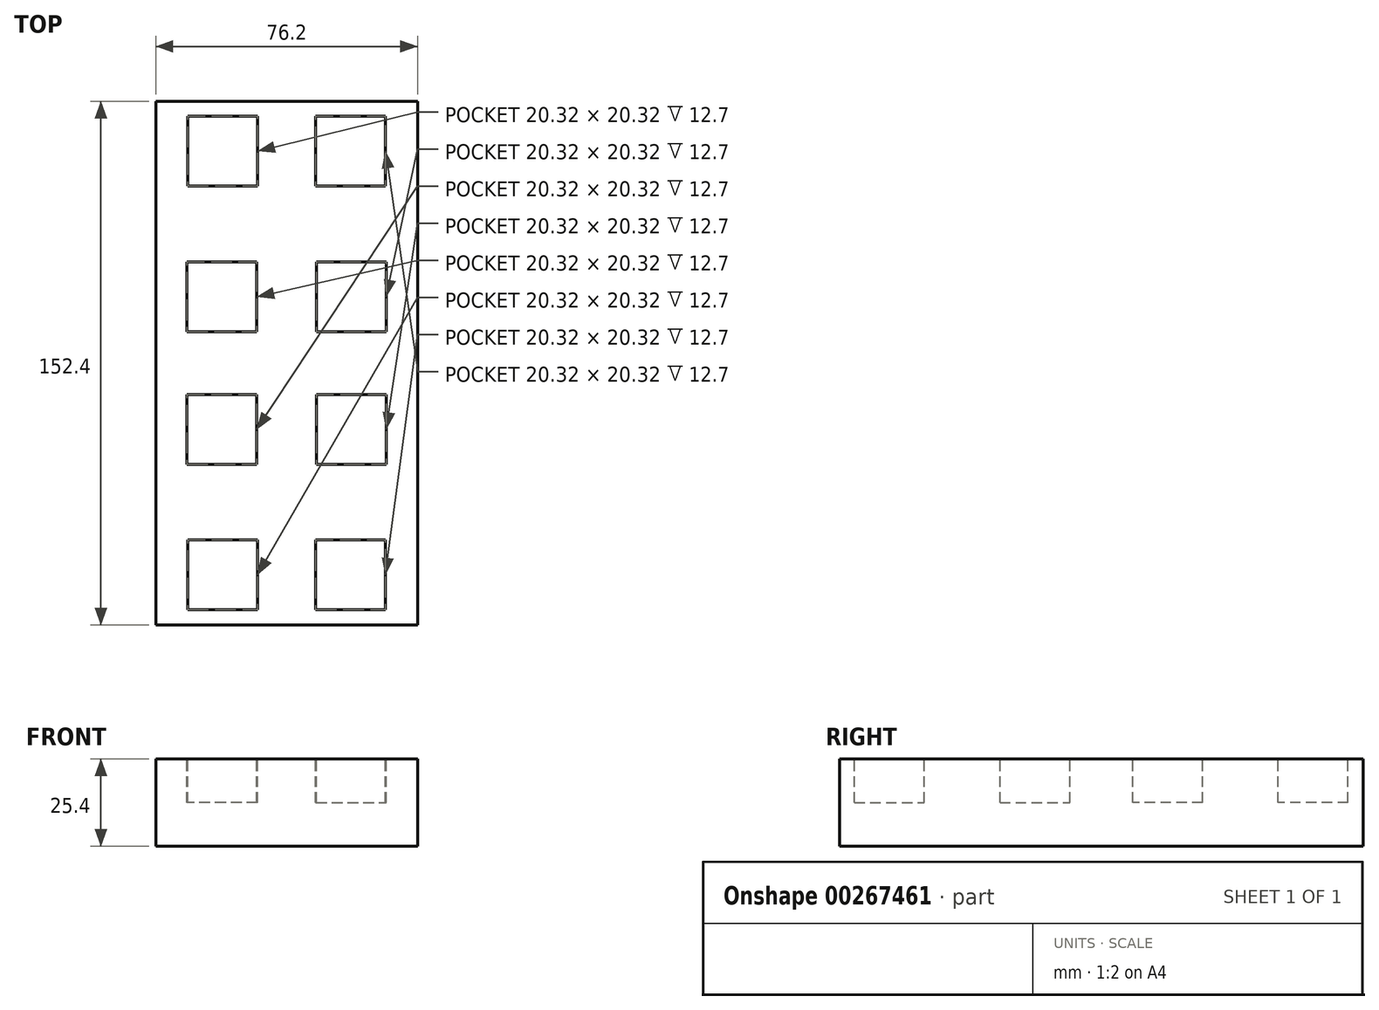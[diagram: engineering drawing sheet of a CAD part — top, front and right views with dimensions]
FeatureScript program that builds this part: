
annotation { "Feature Type Name" : "Feature", "Feature Type Description" : "" }
export const myFeature = defineFeature(function(context is Context, id is Id, definition is map)
    precondition{}
    {
        {
            var Q0;
            Q0=qCreatedBy(makeId("Top.planeOp"),FACE);
            var sketch = newSketch(context, id + "F0", { "sketchPlane" : qUnion([Q0])});
            skLineSegment(sketch, "E0.bottom", {"start": v(38.1, 76.2) * mm, "end": v(-38.1, 76.2) * mm});
            skLineSegment(sketch, "E0.top", {"start": v(38.1, -76.2) * mm, "end": v(-38.1, -76.2) * mm});
            skLineSegment(sketch, "E0.left", {"start": v(38.1, 76.2) * mm, "end": v(38.1, -76.2) * mm});
            skLineSegment(sketch, "E0.right", {"start": v(-38.1, 76.2) * mm, "end": v(-38.1, -76.2) * mm});
            skPoint(sketch, "E0.middle", {"position": v(0, 0) * mm});
            skSolve(sketch);
        }
        {
            var Q0;
            Q0=makeQuery(id+"F0.imprint","IMPRINT",FACE,{"disambiguationData":[TD([[makeQuery(id+"F0.imprint","IMPRINT",EDGE,{"derivedFrom":sQuery(id+"F0.wireOp",EDGE,"E0.bottom")}),1.0]])]});
            extrude(context, id + "F1", {"entities" : qUnion([Q0]), "oppositeDirection" : true, "depth" : 25.4 * mm});
        }
        {
            var Q0;
            Q0=makeQuery(id+"F1.opExtrude","CAP_FACE",FACE,{"disambiguationData":[OSD([sQuery(id+"F0.wireOp",EDGE,"E0.bottom"),sQuery(id+"F0.wireOp",EDGE,"E0.top"),sQuery(id+"F0.wireOp",EDGE,"E0.left"),sQuery(id+"F0.wireOp",EDGE,"E0.right")])],"isStart":true});
            var sketch = newSketch(context, id + "F2", { "sketchPlane" : qUnion([Q0])});
            skLineSegment(sketch, "E1.bottom", {"start": v(-8.46, 71.82) * mm, "end": v(-28.78, 71.82) * mm});
            skLineSegment(sketch, "E1.top", {"start": v(-8.46, 51.5) * mm, "end": v(-28.78, 51.5) * mm});
            skLineSegment(sketch, "E1.left", {"start": v(-8.46, 71.82) * mm, "end": v(-8.46, 51.5) * mm});
            skLineSegment(sketch, "E1.right", {"start": v(-28.78, 71.82) * mm, "end": v(-28.78, 51.5) * mm});
            skPoint(sketch, "E1.middle", {"position": v(-18.62, 61.66) * mm});
            skLineSegment(sketch, "E2.MirrorCS", {"start": v(8.46, 51.5) * mm, "end": v(28.78, 51.5) * mm});
            skLineSegment(sketch, "E3.MirrorCS", {"start": v(8.46, 71.82) * mm, "end": v(8.46, 51.5) * mm});
            skLineSegment(sketch, "E4.MirrorCS", {"start": v(8.46, 71.82) * mm, "end": v(28.78, 71.82) * mm});
            skLineSegment(sketch, "E5.MirrorCS", {"start": v(28.78, 71.82) * mm, "end": v(28.78, 51.5) * mm});
            skLineSegment(sketch, "E6.MirrorCS", {"start": v(8.46, -51.5) * mm, "end": v(28.78, -51.5) * mm});
            skLineSegment(sketch, "E7.MirrorCS", {"start": v(8.46, -71.82) * mm, "end": v(28.78, -71.82) * mm});
            skLineSegment(sketch, "E8.MirrorCS", {"start": v(28.78, -71.82) * mm, "end": v(28.78, -51.5) * mm});
            skLineSegment(sketch, "E9.MirrorCS", {"start": v(8.46, -71.82) * mm, "end": v(8.46, -51.5) * mm});
            skLineSegment(sketch, "E10.MirrorCS", {"start": v(-8.46, -51.5) * mm, "end": v(-28.78, -51.5) * mm});
            skLineSegment(sketch, "E11.MirrorCS", {"start": v(-8.46, -71.82) * mm, "end": v(-8.46, -51.5) * mm});
            skLineSegment(sketch, "E12.MirrorCS", {"start": v(-28.78, -71.82) * mm, "end": v(-28.78, -51.5) * mm});
            skLineSegment(sketch, "E13.MirrorCS", {"start": v(-8.46, -71.82) * mm, "end": v(-28.78, -71.82) * mm});
            skLineSegment(sketch, "E14.bottom", {"start": v(-8.68, 29.48) * mm, "end": v(-29, 29.48) * mm});
            skLineSegment(sketch, "E14.top", {"start": v(-8.68, 9.16) * mm, "end": v(-29, 9.16) * mm});
            skLineSegment(sketch, "E14.left", {"start": v(-8.68, 29.48) * mm, "end": v(-8.68, 9.16) * mm});
            skLineSegment(sketch, "E14.right", {"start": v(-29, 29.48) * mm, "end": v(-29, 9.16) * mm});
            skPoint(sketch, "E14.middle", {"position": v(-18.84, 19.32) * mm});
            skLineSegment(sketch, "E15.MirrorCS", {"start": v(8.68, 29.48) * mm, "end": v(29, 29.48) * mm});
            skLineSegment(sketch, "E16.MirrorCS", {"start": v(29, 29.48) * mm, "end": v(29, 9.16) * mm});
            skLineSegment(sketch, "E17.MirrorCS", {"start": v(8.68, 9.16) * mm, "end": v(29, 9.16) * mm});
            skLineSegment(sketch, "E18.MirrorCS", {"start": v(8.68, 29.48) * mm, "end": v(8.68, 9.16) * mm});
            skLineSegment(sketch, "E19.MirrorCS", {"start": v(-8.68, -9.16) * mm, "end": v(-29, -9.16) * mm});
            skLineSegment(sketch, "E20.MirrorCS", {"start": v(-29, -29.48) * mm, "end": v(-29, -9.16) * mm});
            skLineSegment(sketch, "E21.MirrorCS", {"start": v(-8.68, -29.48) * mm, "end": v(-29, -29.48) * mm});
            skLineSegment(sketch, "E22.MirrorCS", {"start": v(-8.68, -29.48) * mm, "end": v(-8.68, -9.16) * mm});
            skLineSegment(sketch, "E23.MirrorCS", {"start": v(8.68, -29.48) * mm, "end": v(8.68, -9.16) * mm});
            skLineSegment(sketch, "E24.MirrorCS", {"start": v(8.68, -29.48) * mm, "end": v(29, -29.48) * mm});
            skLineSegment(sketch, "E25.MirrorCS", {"start": v(29, -29.48) * mm, "end": v(29, -9.16) * mm});
            skLineSegment(sketch, "E26.MirrorCS", {"start": v(8.68, -9.16) * mm, "end": v(29, -9.16) * mm});
            skSolve(sketch);
        }
        {
            var Q0;
            Q0 = qSketchRegion(id + "F2", true);
            extrude(context, id + "F3", {"entities" : qUnion([Q0]), "operationType" : NewBodyOperationType.REMOVE, "oppositeDirection" : true, "depth" : 12.7 * mm});
        }
    });
